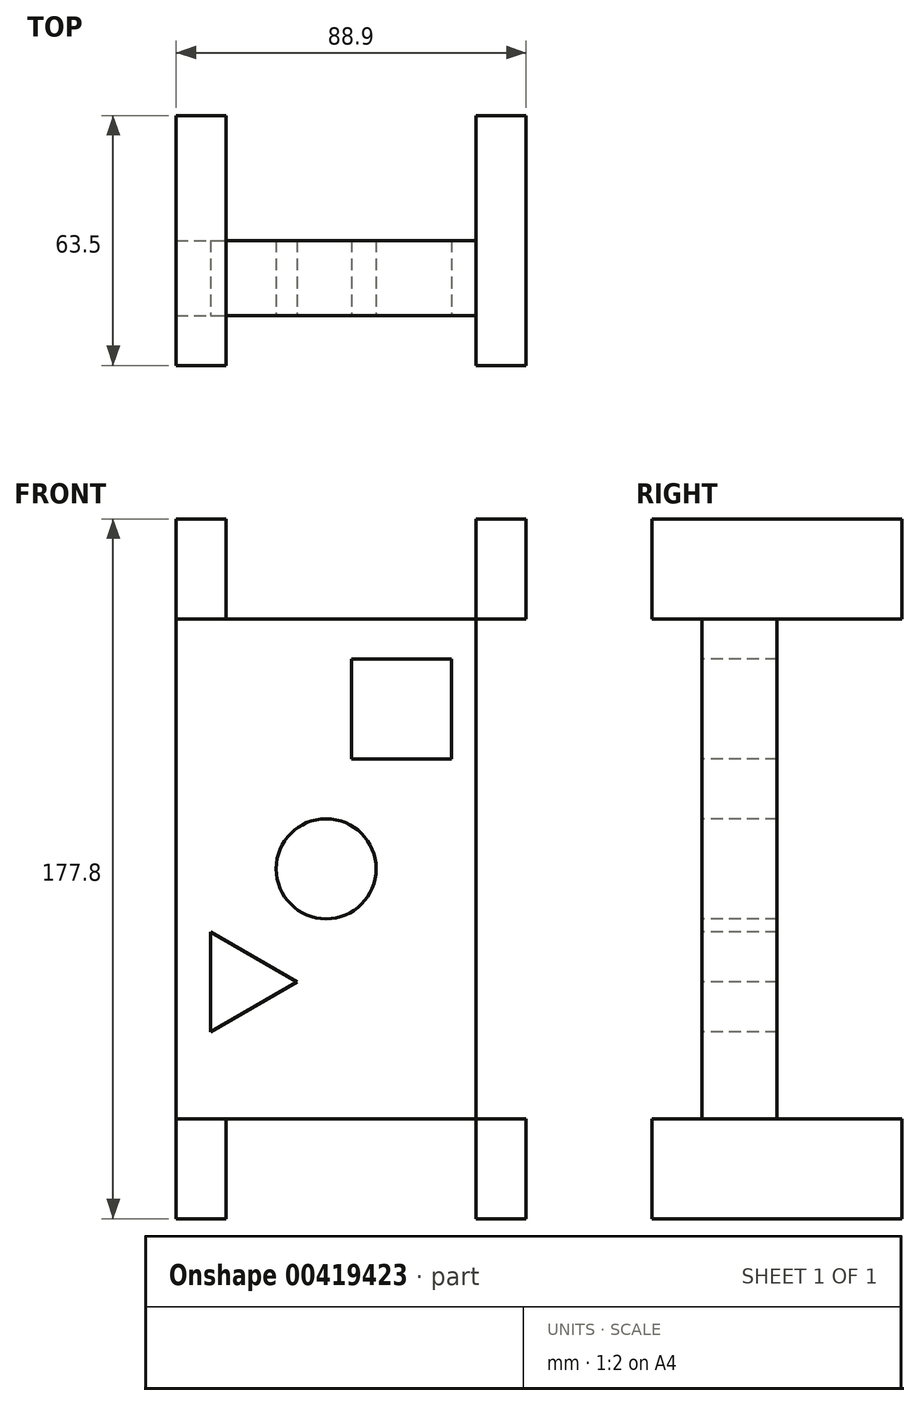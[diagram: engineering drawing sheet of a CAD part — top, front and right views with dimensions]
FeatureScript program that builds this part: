
annotation { "Feature Type Name" : "Feature", "Feature Type Description" : "" }
export const myFeature = defineFeature(function(context is Context, id is Id, definition is map)
    precondition{}
    {
        {
            var Q0;
            Q0=qCreatedBy(makeId("Front.planeOp"),FACE);
            var sketch = newSketch(context, id + "F0", { "sketchPlane" : qUnion([Q0])});
            skLineSegment(sketch, "E0.bottom", {"start": v(-38.1, 63.5) * mm, "end": v(38.1, 63.5) * mm});
            skLineSegment(sketch, "E0.top", {"start": v(-38.1, -63.5) * mm, "end": v(38.1, -63.5) * mm});
            skLineSegment(sketch, "E0.left", {"start": v(-38.1, 63.5) * mm, "end": v(-38.1, -63.5) * mm});
            skLineSegment(sketch, "E0.right", {"start": v(38.1, 63.5) * mm, "end": v(38.1, -63.5) * mm});
            skPoint(sketch, "E0.middle", {"position": v(0, 0) * mm});
            skSolve(sketch);
        }
        {
            var Q0;
            Q0 = qSketchRegion(id + "F0", true);
            extrude(context, id + "F1", {"entities" : qUnion([Q0]), "depth" : 19.05 * mm, "offsetDistance" : 25.4 * mm});
        }
        {
            var Q0;
            Q0=makeQuery(id+"F1.opExtrude","CAP_FACE",FACE,{"disambiguationData":[OSD([sQuery(id+"F0.wireOp",EDGE,"E0.bottom"),sQuery(id+"F0.wireOp",EDGE,"E0.top"),sQuery(id+"F0.wireOp",EDGE,"E0.left"),sQuery(id+"F0.wireOp",EDGE,"E0.right")])],"isStart":false});
            var sketch = newSketch(context, id + "F2", { "sketchPlane" : qUnion([Q0])});
            skLineSegment(sketch, "E1", {"start": v(31.9, 53.34) * mm, "end": v(6.5, 53.34) * mm});
            skLineSegment(sketch, "E2", {"start": v(31.9, 53.34) * mm, "end": v(31.9, 27.94) * mm});
            skLineSegment(sketch, "E3", {"start": v(31.9, 27.94) * mm, "end": v(6.5, 27.94) * mm});
            skLineSegment(sketch, "E4", {"start": v(6.5, 53.34) * mm, "end": v(6.5, 27.94) * mm});
            skSolve(sketch);
        }
        {
            var Q0;
            Q0 = qSketchRegion(id + "F2", true);
            extrude(context, id + "F3", {"entities" : qUnion([Q0]), "operationType" : NewBodyOperationType.REMOVE, "oppositeDirection" : true, "depth" : 50.8 * mm, "offsetDistance" : 25.4 * mm});
        }
        {
            var Q0;
            Q0=makeQuery(id+"F1.opExtrude","CAP_FACE",FACE,{"disambiguationData":[OSD([sQuery(id+"F0.wireOp",EDGE,"E0.bottom"),sQuery(id+"F0.wireOp",EDGE,"E0.top"),sQuery(id+"F0.wireOp",EDGE,"E0.left"),sQuery(id+"F0.wireOp",EDGE,"E0.right")])],"isStart":false});
            var sketch = newSketch(context, id + "F4", { "sketchPlane" : qUnion([Q0])});
            skCircle(sketch, "E5", {"center": v(0, 0) * mm, "radius": 12.7 * mm});
            skSolve(sketch);
        }
        {
            var Q0;
            Q0 = qSketchRegion(id + "F4", true);
            extrude(context, id + "F5", {"entities" : qUnion([Q0]), "operationType" : NewBodyOperationType.REMOVE, "oppositeDirection" : true, "depth" : 50.8 * mm, "offsetDistance" : 25.4 * mm});
        }
        {
            var Q0;
            Q0=makeQuery(id+"F1.opExtrude","CAP_FACE",FACE,{"disambiguationData":[OSD([sQuery(id+"F0.wireOp",EDGE,"E0.bottom"),sQuery(id+"F0.wireOp",EDGE,"E0.top"),sQuery(id+"F0.wireOp",EDGE,"E0.left"),sQuery(id+"F0.wireOp",EDGE,"E0.right")])],"isStart":false});
            var sketch = newSketch(context, id + "F6", { "sketchPlane" : qUnion([Q0])});
            skLineSegment(sketch, "E6", {"start": v(-29.43, -16.06) * mm, "end": v(-29.43, -41.46) * mm});
            skLineSegment(sketch, "E7", {"start": v(-29.43, -16.06) * mm, "end": v(-7.44, -28.76) * mm});
            skLineSegment(sketch, "E8", {"start": v(-7.44, -28.76) * mm, "end": v(-29.43, -41.46) * mm});
            skSolve(sketch);
        }
        {
            var Q0;
            Q0 = qSketchRegion(id + "F6", true);
            extrude(context, id + "F7", {"entities" : qUnion([Q0]), "operationType" : NewBodyOperationType.REMOVE, "oppositeDirection" : true, "depth" : 50.8 * mm, "offsetDistance" : 25.4 * mm});
        }
        {
            var Q0;
            Q0=makeQuery(id+"F1.opExtrude","SWEPT_FACE",FACE,{"disambiguationData":[OSD([sQuery(id+"F0.wireOp",EDGE,"E0.top")])]});
            var sketch = newSketch(context, id + "F8", { "sketchPlane" : qUnion([Q0])});
            skLineSegment(sketch, "E9", {"start": v(-38.1, 19.05) * mm, "end": v(-38.1, 31.75) * mm});
            skLineSegment(sketch, "E10", {"start": v(-38.1, 31.75) * mm, "end": v(-25.4, 31.75) * mm});
            skLineSegment(sketch, "E11", {"start": v(-25.4, 31.75) * mm, "end": v(-25.4, 19.05) * mm});
            skLineSegment(sketch, "E12", {"start": v(-25.4, 19.05) * mm, "end": v(-25.4, -31.75) * mm});
            skLineSegment(sketch, "E13", {"start": v(-25.4, -31.75) * mm, "end": v(-38.1, -31.75) * mm});
            skLineSegment(sketch, "E14", {"start": v(-38.1, -31.75) * mm, "end": v(-38.1, 19.05) * mm});
            skSolve(sketch);
        }
        {
            var Q0;
            Q0 = qSketchRegion(id + "F8", true);
            extrude(context, id + "F9", {"entities" : qUnion([Q0]), "operationType" : NewBodyOperationType.ADD, "depth" : 25.4 * mm, "offsetDistance" : 25.4 * mm});
        }
        {
            var Q0;
            Q0=makeQuery(id+"F1.opExtrude","SWEPT_FACE",FACE,{"disambiguationData":[OSD([sQuery(id+"F0.wireOp",EDGE,"E0.bottom")])]});
            var sketch = newSketch(context, id + "F10", { "sketchPlane" : qUnion([Q0])});
            skLineSegment(sketch, "E15", {"start": v(-25.4, -31.75) * mm, "end": v(-25.4, -19.05) * mm});
            skLineSegment(sketch, "E16", {"start": v(-25.4, -31.75) * mm, "end": v(-38.1, -31.75) * mm});
            skLineSegment(sketch, "E17", {"start": v(-38.1, -31.75) * mm, "end": v(-38.1, -19.05) * mm});
            skLineSegment(sketch, "E18", {"start": v(-38.1, -19.05) * mm, "end": v(-38.1, 31.75) * mm});
            skLineSegment(sketch, "E19", {"start": v(-38.1, 31.75) * mm, "end": v(-25.4, 31.75) * mm});
            skLineSegment(sketch, "E20", {"start": v(-25.4, 31.75) * mm, "end": v(-25.4, -19.05) * mm});
            skSolve(sketch);
        }
        {
            var Q0;
            Q0 = qSketchRegion(id + "F10", true);
            extrude(context, id + "F11", {"entities" : qUnion([Q0]), "operationType" : NewBodyOperationType.ADD, "depth" : 25.4 * mm, "offsetDistance" : 25.4 * mm});
        }
        {
            var Q0;
            Q0=makeQuery(id+"F1.opExtrude","SWEPT_FACE",FACE,{"disambiguationData":[OSD([sQuery(id+"F0.wireOp",EDGE,"E0.top")])]});
            var sketch = newSketch(context, id + "F12", { "sketchPlane" : qUnion([Q0])});
            skLineSegment(sketch, "E21", {"start": v(38.1, 19.05) * mm, "end": v(38.1, 31.75) * mm});
            skLineSegment(sketch, "E22", {"start": v(38.1, 31.75) * mm, "end": v(50.8, 31.75) * mm});
            skLineSegment(sketch, "E23", {"start": v(50.8, 31.75) * mm, "end": v(50.8, -31.75) * mm});
            skLineSegment(sketch, "E24", {"start": v(38.1, 19.05) * mm, "end": v(38.1, -31.75) * mm});
            skLineSegment(sketch, "E25", {"start": v(38.1, -31.75) * mm, "end": v(50.8, -31.75) * mm});
            skSolve(sketch);
        }
        {
            var Q0;
            Q0 = qSketchRegion(id + "F12", true);
            extrude(context, id + "F13", {"entities" : qUnion([Q0]), "depth" : 25.4 * mm, "offsetDistance" : 25.4 * mm});
        }
        {
            var Q0;
            Q0=makeQuery(id+"F1.opExtrude","SWEPT_FACE",FACE,{"disambiguationData":[OSD([sQuery(id+"F0.wireOp",EDGE,"E0.right")])]});
            var sketch = newSketch(context, id + "F14", { "sketchPlane" : qUnion([Q0])});
            skLineSegment(sketch, "E26", {"start": v(-19.05, 63.5) * mm, "end": v(-31.75, 63.5) * mm});
            skLineSegment(sketch, "E27", {"start": v(-31.75, 63.5) * mm, "end": v(-31.75, 88.9) * mm});
            skLineSegment(sketch, "E28", {"start": v(-31.75, 88.9) * mm, "end": v(31.75, 88.9) * mm});
            skLineSegment(sketch, "E29", {"start": v(31.75, 88.9) * mm, "end": v(31.75, 63.5) * mm});
            skLineSegment(sketch, "E30", {"start": v(31.75, 63.5) * mm, "end": v(-19.05, 63.5) * mm});
            skSolve(sketch);
        }
        {
            var Q0;
            Q0 = qSketchRegion(id + "F14", true);
            extrude(context, id + "F15", {"entities" : qUnion([Q0]), "depth" : 12.7 * mm, "offsetDistance" : 25.4 * mm});
        }
    });
